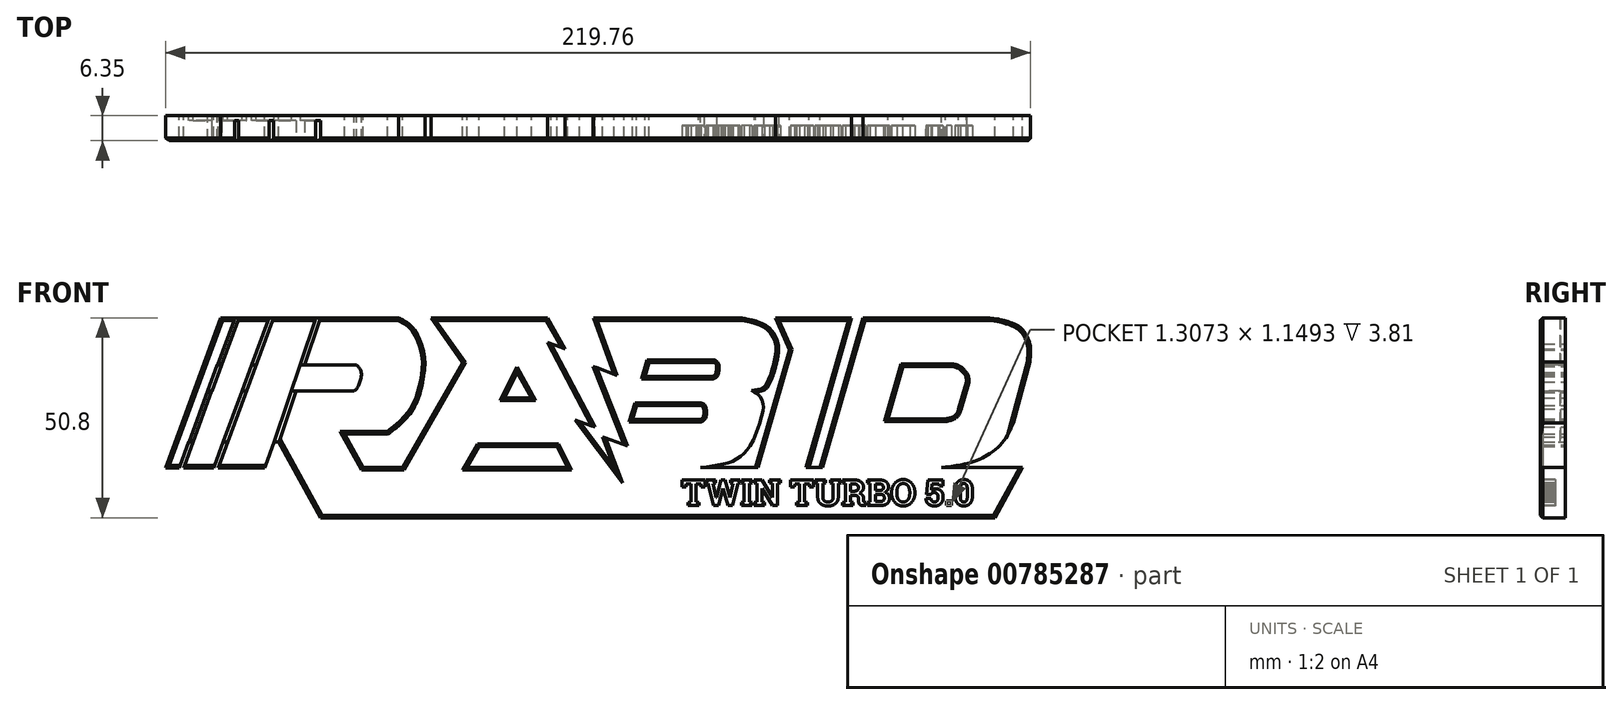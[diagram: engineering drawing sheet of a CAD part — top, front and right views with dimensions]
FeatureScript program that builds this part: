
annotation { "Feature Type Name" : "Feature", "Feature Type Description" : "" }
export const myFeature = defineFeature(function(context is Context, id is Id, definition is map)
    precondition{}
    {
        {
            var Q0;
            Q0=qCreatedBy(makeId("Front.planeOp"),FACE);
            var sketch = newSketch(context, id + "F0", { "sketchPlane" : qUnion([Q0])});
            skLineSegment(sketch, "E0", {"start": v(44.45, 18.23) * mm, "end": v(13.33, 18.23) * mm});
            skLineSegment(sketch, "E1", {"start": v(-163.82, -19.93) * mm, "end": v(-149.78, 18.23) * mm});
            skLineSegment(sketch, "E2", {"start": v(-138.67, -19.93) * mm, "end": v(-150.42, -19.93) * mm});
            skLineSegment(sketch, "E3", {"start": v(-146.28, 18.23) * mm, "end": v(-160.32, -19.93) * mm});
            skLineSegment(sketch, "E4", {"start": v(-159.23, -19.93) * mm, "end": v(-145.19, 18.23) * mm});
            skLineSegment(sketch, "E5", {"start": v(-137.53, 18.23) * mm, "end": v(-151.57, -19.93) * mm});
            skLineSegment(sketch, "E6", {"start": v(-150.42, -19.93) * mm, "end": v(-136.37, 18.23) * mm});
            skLineSegment(sketch, "E7", {"start": v(-124.63, 18.23) * mm, "end": v(-138.67, -19.93) * mm});
            skLineSegment(sketch, "E8", {"start": v(-127.97, 6.26) * mm, "end": v(-123.56, 18.23) * mm});
            skLineSegment(sketch, "E9", {"start": v(-127.97, 6.26) * mm, "end": v(-115.24, 6.26) * mm});
            skLineSegment(sketch, "E10", {"start": v(-115.92, -0.4) * mm, "end": v(-130.28, -0.4) * mm});
            skLineSegment(sketch, "E11", {"start": v(-130.28, -0.4) * mm, "end": v(-135.05, -13.36) * mm});
            skLineSegment(sketch, "E12", {"start": v(-135.05, -13.36) * mm, "end": v(-124.47, -32.57) * mm});
            skLineSegment(sketch, "E13", {"start": v(-124.47, -32.57) * mm, "end": v(-110.55, -32.57) * mm});
            skLineSegment(sketch, "E14", {"start": v(-110.55, -32.57) * mm, "end": v(-103.65, -19.74) * mm});
            skLineSegment(sketch, "E15", {"start": v(-103.65, -19.74) * mm, "end": v(-113.7, -19.74) * mm});
            skLineSegment(sketch, "E16", {"start": v(-113.7, -19.74) * mm, "end": v(-118.36, -11.28) * mm});
            skLineSegment(sketch, "E17", {"start": v(-118.36, -11.28) * mm, "end": v(-107.38, -11.28) * mm});
            skLineSegment(sketch, "E18", {"start": v(-103.65, -19.74) * mm, "end": v(-87.29, -19.74) * mm});
            skLineSegment(sketch, "E19", {"start": v(-96.42, 18.23) * mm, "end": v(-88.35, 6.81) * mm});
            skLineSegment(sketch, "E20", {"start": v(-88.35, 6.81) * mm, "end": v(-103.65, -19.74) * mm});
            skLineSegment(sketch, "E21", {"start": v(-87.29, -19.74) * mm, "end": v(-84.2, -14.4) * mm});
            skLineSegment(sketch, "E22", {"start": v(-84.2, -14.4) * mm, "end": v(-64.33, -14.4) * mm});
            skLineSegment(sketch, "E23", {"start": v(-64.33, -14.4) * mm, "end": v(-61.66, -19.74) * mm});
            skLineSegment(sketch, "E24", {"start": v(-66.84, 18.23) * mm, "end": v(-62.3, 10.3) * mm});
            skLineSegment(sketch, "E25", {"start": v(-62.3, 10.3) * mm, "end": v(-65.92, 11.65) * mm});
            skLineSegment(sketch, "E26", {"start": v(-65.92, 11.65) * mm, "end": v(-54.7, -9.5) * mm});
            skLineSegment(sketch, "E27", {"start": v(-54.7, -9.5) * mm, "end": v(-58.68, -8.06) * mm});
            skLineSegment(sketch, "E28", {"start": v(-58.68, -8.06) * mm, "end": v(-49.86, -19.74) * mm});
            skLineSegment(sketch, "E29", {"start": v(-70.89, -2.18) * mm, "end": v(-77.76, -2.18) * mm});
            skLineSegment(sketch, "E30", {"start": v(-77.76, -2.18) * mm, "end": v(-74.5, 4.32) * mm});
            skLineSegment(sketch, "E31", {"start": v(-74.5, 4.32) * mm, "end": v(-70.89, -2.18) * mm});
            skLineSegment(sketch, "E32", {"start": v(-55.14, 18.23) * mm, "end": v(-49.92, 3.87) * mm});
            skLineSegment(sketch, "E33", {"start": v(-49.92, 3.87) * mm, "end": v(-55.16, 5.86) * mm});
            skLineSegment(sketch, "E34", {"start": v(-55.16, 5.86) * mm, "end": v(-47.3, -14.02) * mm});
            skLineSegment(sketch, "E35", {"start": v(-47.3, -14.02) * mm, "end": v(-52.8, -12.04) * mm});
            skLineSegment(sketch, "E36", {"start": v(-52.8, -12.04) * mm, "end": v(-49.86, -19.74) * mm});
            skLineSegment(sketch, "E37", {"start": v(-40.97, 6.88) * mm, "end": v(-42, 3.36) * mm});
            skLineSegment(sketch, "E38", {"start": v(-45.2, -7.65) * mm, "end": v(-28.43, -7.65) * mm});
            skLineSegment(sketch, "E39", {"start": v(-44.14, -3.97) * mm, "end": v(-28.03, -3.97) * mm});
            skLineSegment(sketch, "E40", {"start": v(-40.97, 6.88) * mm, "end": v(-24.6, 6.88) * mm});
            skLineSegment(sketch, "E41", {"start": v(-42, 3.36) * mm, "end": v(-25, 3.36) * mm});
            skLineSegment(sketch, "E42", {"start": v(-8.93, 18.23) * mm, "end": v(-5.34, 10.12) * mm});
            skLineSegment(sketch, "E43", {"start": v(-5.34, 10.12) * mm, "end": v(-13.99, -19.74) * mm});
            skLineSegment(sketch, "E44", {"start": v(10.46, 18.23) * mm, "end": v(-0.4, -19.74) * mm});
            skLineSegment(sketch, "E45", {"start": v(13.33, 18.23) * mm, "end": v(2.47, -19.74) * mm});
            skLineSegment(sketch, "E46", {"start": v(35.81, 5.9) * mm, "end": v(23.48, 5.9) * mm});
            skLineSegment(sketch, "E47", {"start": v(23.48, 5.9) * mm, "end": v(19.66, -7.49) * mm});
            skLineSegment(sketch, "E48", {"start": v(19.66, -7.49) * mm, "end": v(34.3, -7.49) * mm});
            skLineSegment(sketch, "E49", {"start": v(39.6, 1.92) * mm, "end": v(37.65, -4.94) * mm});
            skFitSpline(sketch, "E50", {"points": [v(55.73, 7.05) * mm, v(55.73, 11.7) * mm, v(53.74, 15.4) * mm, v(50.9, 17) * mm, v(44.45, 18.23) * mm], "startDerivative": vector(2.3, 18.78) * mm, "endDerivative": vector(-24.45, 0) * mm});
            skLineSegment(sketch, "E51", {"start": v(55.73, 7.05) * mm, "end": v(51.56, -8.5) * mm});
            skFitSpline(sketch, "E52", {"points": [v(-14.17, -0.73) * mm, v(-12.02, -0.26) * mm, v(-10.54, 1.23) * mm, v(-8.14, 9.39) * mm, v(-8.72, 13.21) * mm, v(-10.35, 15.5) * mm, v(-13.7, 17.35) * mm, v(-18.93, 18.23) * mm], "startDerivative": vector(20.2, 3.41) * mm, "endDerivative": vector(-28.09, 0) * mm});
            skFitSpline(sketch, "E53", {"points": [v(-14.17, -0.73) * mm, v(-12.8, -1.84) * mm, v(-11.95, -3.81) * mm, v(-12.1, -5.72) * mm, v(-14.99, -13.75) * mm, v(-17.24, -16.5) * mm, v(-19.85, -18.27) * mm, v(-23.1, -19.11) * mm, v(-27.89, -19.74) * mm], "startDerivative": vector(16.43, -10.07) * mm, "endDerivative": vector(-33.98, 0) * mm});
            skFitSpline(sketch, "E54", {"points": [v(-24.6, 6.88) * mm, v(-24.2, 6.68) * mm, v(-23.87, 6.14) * mm, v(-24.05, 4.06) * mm, v(-24.29, 3.61) * mm, v(-25, 3.36) * mm], "startDerivative": vector(3.09, 0) * mm, "endDerivative": vector(-4.49, 0) * mm});
            skFitSpline(sketch, "E55", {"points": [v(-28.03, -3.97) * mm, v(-27.5, -4.2) * mm, v(-27.12, -4.85) * mm, v(-27.1, -6.65) * mm, v(-27.44, -7.25) * mm, v(-28.43, -7.65) * mm], "startDerivative": vector(3.73, 0) * mm, "endDerivative": vector(-8.7, -0.89) * mm});
            skFitSpline(sketch, "E56", {"points": [v(-104.57, 18.23) * mm, v(-101.7, 16.39) * mm, v(-99.55, 13.37) * mm, v(-98.04, 8.28) * mm, v(-98.33, 2.83) * mm, v(-99.98, -3.05) * mm, v(-103.2, -7.86) * mm, v(-107.38, -11.28) * mm], "startDerivative": vector(25.95, -13.02) * mm, "endDerivative": vector(-29.28, -21.25) * mm});
            skFitSpline(sketch, "E57", {"points": [v(35.81, 5.9) * mm, v(37.17, 5.6) * mm, v(38.23, 4.97) * mm, v(39.07, 4.03) * mm, v(39.6, 1.92) * mm], "startDerivative": vector(5.58, 0) * mm, "endDerivative": vector(-1.33, -10.82) * mm});
            skFitSpline(sketch, "E58", {"points": [v(34.3, -7.49) * mm, v(35.48, -7.2) * mm, v(36.57, -6.77) * mm, v(37.26, -5.96) * mm, v(37.65, -4.94) * mm], "startDerivative": vector(4.57, 1.01) * mm, "endDerivative": vector(1.33, 4.26) * mm});
            skLineSegment(sketch, "E59.trimOffspring", {"start": v(-146.28, 18.23) * mm, "end": v(-149.78, 18.23) * mm});
            skLineSegment(sketch, "E60.trimOffspring", {"start": v(-137.53, 18.23) * mm, "end": v(-145.19, 18.23) * mm});
            skLineSegment(sketch, "E61.trimOffspring", {"start": v(-124.63, 18.23) * mm, "end": v(-136.37, 18.23) * mm});
            skLineSegment(sketch, "E62.trimOffspring", {"start": v(-104.57, 18.23) * mm, "end": v(-123.56, 18.23) * mm});
            skLineSegment(sketch, "E63.trimOffspring", {"start": v(-151.57, -19.93) * mm, "end": v(-159.23, -19.93) * mm});
            skLineSegment(sketch, "E64.trimOffspring", {"start": v(-160.32, -19.93) * mm, "end": v(-163.82, -19.93) * mm});
            skLineSegment(sketch, "E65.trimOffspring", {"start": v(-61.66, -19.74) * mm, "end": v(-49.86, -19.74) * mm});
            skLineSegment(sketch, "E66.trimOffspring", {"start": v(-49.86, -19.74) * mm, "end": v(-27.89, -19.74) * mm});
            skLineSegment(sketch, "E67.trimOffspring", {"start": v(-66.84, 18.23) * mm, "end": v(-96.42, 18.23) * mm});
            skLineSegment(sketch, "E68.trimOffspring", {"start": v(-44.14, -3.97) * mm, "end": v(-45.2, -7.65) * mm});
            skLineSegment(sketch, "E69.trimOffspring", {"start": v(-18.93, 18.23) * mm, "end": v(-55.14, 18.23) * mm});
            skLineSegment(sketch, "E70.trimOffspring", {"start": v(-13.99, -19.74) * mm, "end": v(-0.4, -19.74) * mm});
            skLineSegment(sketch, "E71.trimOffspring", {"start": v(2.47, -19.74) * mm, "end": v(33.3, -19.74) * mm});
            skLineSegment(sketch, "E72.trimOffspring", {"start": v(10.46, 18.23) * mm, "end": v(-8.93, 18.23) * mm});
            skFitSpline(sketch, "E73", {"points": [v(51.56, -8.5) * mm, v(50.36, -11.15) * mm, v(48.41, -13.9) * mm, v(45.57, -16.27) * mm, v(42.49, -17.92) * mm, v(38.84, -18.97) * mm, v(33.3, -19.74) * mm], "startDerivative": vector(-7.47, -18.05) * mm, "endDerivative": vector(-28.9, 0) * mm});
            skFitSpline(sketch, "E74", {"points": [v(-115.24, 6.26) * mm, v(-114.2, 4.72) * mm, v(-114.26, 2.54) * mm, v(-115.24, 0.25) * mm, v(-115.92, -0.4) * mm], "startDerivative": vector(5.02, -5.67) * mm, "endDerivative": vector(-3.78, -2.78) * mm});
            skLineSegment(sketch, "E75", {"start": v(-87.29, -19.74) * mm, "end": v(-61.66, -19.74) * mm});
            skLineSegment(sketch, "E76", {"start": v(-27.89, -19.74) * mm, "end": v(-13.99, -19.74) * mm});
            skLineSegment(sketch, "E77", {"start": v(-0.4, -19.74) * mm, "end": v(2.47, -19.74) * mm});
            skLineSegment(sketch, "E78", {"start": v(27.98, -32.57) * mm, "end": v(-110.55, -32.57) * mm});
            skLineSegment(sketch, "E79", {"start": v(27.98, -32.57) * mm, "end": v(46.92, -32.57) * mm});
            skLineSegment(sketch, "E80", {"start": v(46.92, -32.57) * mm, "end": v(53.92, -19.74) * mm});
            skLineSegment(sketch, "E81", {"start": v(33.3, -19.74) * mm, "end": v(53.92, -19.74) * mm});
            skLineSegment(sketch, "E82", {"start": v(-123.56, 18.23) * mm, "end": v(-124.63, 18.23) * mm});
            skLineSegment(sketch, "E83", {"start": v(-136.37, 18.23) * mm, "end": v(-137.53, 18.23) * mm});
            skLineSegment(sketch, "E84", {"start": v(-127.97, 6.26) * mm, "end": v(-129.04, 6.26) * mm});
            skLineSegment(sketch, "E85", {"start": v(-130.28, -0.4) * mm, "end": v(-131.49, -0.4) * mm});
            skLineSegment(sketch, "E86", {"start": v(-145.19, 18.23) * mm, "end": v(-146.28, 18.23) * mm});
            skLineSegment(sketch, "E87", {"start": v(-140.78, 6.26) * mm, "end": v(-141.94, 6.26) * mm});
            skLineSegment(sketch, "E88", {"start": v(-149.6, 6.26) * mm, "end": v(-150.69, 6.26) * mm});
            skLineSegment(sketch, "E89", {"start": v(-143.23, -0.4) * mm, "end": v(-144.39, -0.4) * mm});
            skLineSegment(sketch, "E90", {"start": v(-152.05, -0.4) * mm, "end": v(-153.14, -0.4) * mm});
            skLineSegment(sketch, "E91", {"start": v(-130.28, -0.4) * mm, "end": v(-127.97, 6.26) * mm});
            skLineSegment(sketch, "E92", {"start": v(-135.05, -13.36) * mm, "end": v(-136.25, -13.36) * mm});
            skLineSegment(sketch, "E93", {"start": v(-148, -13.36) * mm, "end": v(-149.15, -13.36) * mm});
            skLineSegment(sketch, "E94", {"start": v(-156.81, -13.36) * mm, "end": v(-157.9, -13.36) * mm});
            skSolve(sketch);
        }
        {
            var Q0;
            Q0=qSketchRegion(id+"F0",true);
            extrude(context, id + "F1", {"entities" : qUnion([Q0]), "depth" : 6.35 * mm, "offsetDistance" : 25.4 * mm});
        }
        {
            var Q0;
            {var subQ0=sQuery(id+"F0.wireOp",EDGE,"E30");var subQ1=sQuery(id+"F0.wireOp",EDGE,"E29");var subQ2=sQuery(id+"F0.wireOp",EDGE,"E27");var subQ3=sQuery(id+"F0.wireOp",EDGE,"E24");var subQ4=sQuery(id+"F0.wireOp",EDGE,"E23");var subQ5=sQuery(id+"F0.wireOp",EDGE,"E22");var subQ6=sQuery(id+"F0.wireOp",EDGE,"E21");var subQ7=sQuery(id+"F0.wireOp",EDGE,"E20");var subQ8=sQuery(id+"F0.wireOp",EDGE,"E19");var subQ9=sQuery(id+"F0.wireOp",EDGE,"E17");var subQ10=sQuery(id+"F0.wireOp",EDGE,"E16");var subQ11=sQuery(id+"F0.wireOp",EDGE,"E15");var subQ12=sQuery(id+"F0.wireOp",EDGE,"E79");var subQ13=sQuery(id+"F0.wireOp",EDGE,"E78");var subQ14=sQuery(id+"F0.wireOp",EDGE,"E13");var subQ15=sQuery(id+"F0.wireOp",EDGE,"E12");var subQ16=sQuery(id+"F0.wireOp",EDGE,"E85");var subQ17=sQuery(id+"F0.wireOp",EDGE,"E10");var subQ18=sQuery(id+"F0.wireOp",EDGE,"E84");var subQ19=sQuery(id+"F0.wireOp",EDGE,"E9");var subQ20=sQuery(id+"F0.wireOp",EDGE,"E7");var subQ21=sQuery(id+"F0.wireOp",EDGE,"E2");var subQ22=sQuery(id+"F0.wireOp",EDGE,"E92");var subQ23=sQuery(id+"F0.wireOp",EDGE,"E87");var subQ24=sQuery(id+"F0.wireOp",EDGE,"E6");var subQ25=sQuery(id+"F0.wireOp",EDGE,"E89");var subQ26=sQuery(id+"F0.wireOp",EDGE,"E93");var subQ27=sQuery(id+"F0.wireOp",EDGE,"E63.trimOffspring");var subQ28=sQuery(id+"F0.wireOp",EDGE,"E5");var subQ29=sQuery(id+"F0.wireOp",EDGE,"E88");var subQ30=sQuery(id+"F0.wireOp",EDGE,"E4");var subQ31=sQuery(id+"F0.wireOp",EDGE,"E90");var subQ32=sQuery(id+"F0.wireOp",EDGE,"E94");var subQ33=sQuery(id+"F0.wireOp",EDGE,"E64.trimOffspring");var subQ34=sQuery(id+"F0.wireOp",EDGE,"E3");var subQ35=sQuery(id+"F0.wireOp",EDGE,"E1");var subQ36=sQuery(id+"F0.wireOp",EDGE,"E0");var subQ37=sQuery(id+"F0.wireOp",EDGE,"E81");var subQ38=sQuery(id+"F0.wireOp",EDGE,"E80");var subQ39=sQuery(id+"F0.wireOp",EDGE,"E76");var subQ40=sQuery(id+"F0.wireOp",EDGE,"E75");var subQ41=sQuery(id+"F0.wireOp",EDGE,"E74");var subQ42=sQuery(id+"F0.wireOp",EDGE,"E73");var subQ43=sQuery(id+"F0.wireOp",EDGE,"E72.trimOffspring");var subQ44=sQuery(id+"F0.wireOp",EDGE,"E69.trimOffspring");var subQ45=sQuery(id+"F0.wireOp",EDGE,"E68.trimOffspring");var subQ46=sQuery(id+"F0.wireOp",EDGE,"E48");var subQ47=sQuery(id+"F0.wireOp",EDGE,"E77");var subQ48=sQuery(id+"F0.wireOp",EDGE,"E47");var subQ49=sQuery(id+"F0.wireOp",EDGE,"E45");var subQ50=sQuery(id+"F0.wireOp",EDGE,"E50");var subQ51=sQuery(id+"F0.wireOp",EDGE,"E28");var subQ52=sQuery(id+"F0.wireOp",EDGE,"E49");var subQ53=sQuery(id+"F0.wireOp",EDGE,"E46");var subQ54=sQuery(id+"F0.wireOp",EDGE,"E55");var subQ55=sQuery(id+"F0.wireOp",EDGE,"E41");var subQ56=sQuery(id+"F0.wireOp",EDGE,"E40");var subQ57=sQuery(id+"F0.wireOp",EDGE,"E32");var subQ58=sQuery(id+"F0.wireOp",EDGE,"E31");var subQ59=sQuery(id+"F0.wireOp",EDGE,"E33");var subQ60=sQuery(id+"F0.wireOp",EDGE,"E51");var subQ61=sQuery(id+"F0.wireOp",EDGE,"E44");var subQ62=sQuery(id+"F0.wireOp",EDGE,"E39");var subQ63=sQuery(id+"F0.wireOp",EDGE,"E34");var subQ64=sQuery(id+"F0.wireOp",EDGE,"E35");var subQ65=sQuery(id+"F0.wireOp",EDGE,"E36");var subQ66=sQuery(id+"F0.wireOp",EDGE,"E37");var subQ67=sQuery(id+"F0.wireOp",EDGE,"E38");var subQ68=sQuery(id+"F0.wireOp",EDGE,"E52");var subQ69=sQuery(id+"F0.wireOp",EDGE,"E53");var subQ70=sQuery(id+"F0.wireOp",EDGE,"E54");var subQ71=sQuery(id+"F0.wireOp",EDGE,"E56");var subQ72=sQuery(id+"F0.wireOp",EDGE,"E25");var subQ73=sQuery(id+"F0.wireOp",EDGE,"E57");var subQ74=sQuery(id+"F0.wireOp",EDGE,"E26");var subQ75=sQuery(id+"F0.wireOp",EDGE,"E58");var subQ76=sQuery(id+"F0.wireOp",EDGE,"E86");var subQ77=sQuery(id+"F0.wireOp",EDGE,"E83");var subQ78=sQuery(id+"F0.wireOp",EDGE,"E82");var subQ79=sQuery(id+"F0.wireOp",EDGE,"E62.trimOffspring");var subQ80=sQuery(id+"F0.wireOp",EDGE,"E61.trimOffspring");var subQ81=sQuery(id+"F0.wireOp",EDGE,"E60.trimOffspring");var subQ82=sQuery(id+"F0.wireOp",EDGE,"E59.trimOffspring");var subQ83=sQuery(id+"F0.wireOp",EDGE,"E67.trimOffspring");var subQ84=sQuery(id+"F0.wireOp",EDGE,"E42");var subQ85=sQuery(id+"F0.wireOp",EDGE,"E43");Q0=makeQuery(id+"F5.boolean.opBoolean","SPLIT",FACE,{"disambiguationData":[TD([makeQuery(id+"F1.opExtrude","SWEPT_FACE",FACE,{"disambiguationData":[OSD([subQ36])]})])],"derivedFrom":makeQuery(id+"F1.opExtrude","CAP_FACE",FACE,{"disambiguationData":[OSD([subQ36,subQ35,subQ21,subQ34,subQ30,subQ28,subQ24,subQ20,subQ19,subQ17,subQ15,subQ14,subQ11,subQ10,subQ9,subQ8,subQ7,subQ6,subQ5,subQ4,subQ3,subQ72,subQ74,subQ2,subQ51,subQ1,subQ0,subQ58,subQ57,subQ59,subQ63,subQ64,subQ65,subQ66,subQ67,subQ62,subQ56,subQ55,subQ84,subQ85,subQ61,subQ49,subQ53,subQ48,subQ46,subQ52,subQ50,subQ60,subQ68,subQ69,subQ70,subQ54,subQ71,subQ73,subQ75,subQ82,subQ81,subQ80,subQ79,subQ27,subQ33,subQ83,subQ45,subQ44,subQ43,subQ42,subQ41,subQ40,subQ39,subQ47,subQ13,subQ12,subQ38,subQ37,subQ78,subQ77,subQ18,subQ16,subQ76,subQ23,subQ29,subQ25,subQ31,subQ22,subQ26,subQ32])],"isStart":false})});}
            var sketch = newSketch(context, id + "F2", { "sketchPlane" : qUnion([Q0])});
            skLineSegment(sketch, "E95", {"start": v(-160.32, -19.93) * mm, "end": v(-159.23, -19.93) * mm});
            skLineSegment(sketch, "E96", {"start": v(-159.23, -19.93) * mm, "end": v(-145.22, 18.23) * mm});
            skLineSegment(sketch, "E97", {"start": v(-145.22, 18.23) * mm, "end": v(-146.23, 18.23) * mm});
            skLineSegment(sketch, "E98", {"start": v(-146.23, 18.23) * mm, "end": v(-160.32, -19.93) * mm});
            skLineSegment(sketch, "E99", {"start": v(-151.57, -19.93) * mm, "end": v(-150.42, -19.93) * mm});
            skLineSegment(sketch, "E100", {"start": v(-150.42, -19.93) * mm, "end": v(-136.37, 18.23) * mm});
            skLineSegment(sketch, "E101", {"start": v(-136.37, 18.23) * mm, "end": v(-137.53, 18.23) * mm});
            skLineSegment(sketch, "E102", {"start": v(-137.53, 18.23) * mm, "end": v(-151.57, -19.93) * mm});
            skPoint(sketch, "E103.endSnap0", {"position": v(-129.76, -22.96) * mm});
            skLineSegment(sketch, "E104", {"start": v(-136.25, -13.36) * mm, "end": v(-135.05, -13.36) * mm});
            skLineSegment(sketch, "E105", {"start": v(-135.05, -13.36) * mm, "end": v(-124.47, 18.23) * mm});
            skLineSegment(sketch, "E106", {"start": v(-124.47, 18.23) * mm, "end": v(-125.67, 18.23) * mm});
            skLineSegment(sketch, "E107", {"start": v(-125.67, 18.23) * mm, "end": v(-136.25, -13.36) * mm});
            skSolve(sketch);
        }
        {
            var Q0;
            Q0=qSketchRegion(id+"F2",true);
            extrude(context, id + "F3", {"entities" : qUnion([Q0]), "operationType" : NewBodyOperationType.REMOVE, "oppositeDirection" : true, "depth" : 5.08 * mm, "offsetDistance" : 25.4 * mm});
        }
        {
            var Q0;
            Q0=makeQuery(id+"F1.opExtrude","CAP_FACE",FACE,{"disambiguationData":[OSD([sQuery(id+"F0.wireOp",EDGE,"E0"),sQuery(id+"F0.wireOp",EDGE,"E8"),sQuery(id+"F0.wireOp",EDGE,"E9"),sQuery(id+"F0.wireOp",EDGE,"E10"),sQuery(id+"F0.wireOp",EDGE,"E11"),sQuery(id+"F0.wireOp",EDGE,"E12"),sQuery(id+"F0.wireOp",EDGE,"E13"),sQuery(id+"F0.wireOp",EDGE,"E15"),sQuery(id+"F0.wireOp",EDGE,"E16"),sQuery(id+"F0.wireOp",EDGE,"E17"),sQuery(id+"F0.wireOp",EDGE,"E19"),sQuery(id+"F0.wireOp",EDGE,"E20"),sQuery(id+"F0.wireOp",EDGE,"E21"),sQuery(id+"F0.wireOp",EDGE,"E22"),sQuery(id+"F0.wireOp",EDGE,"E23"),sQuery(id+"F0.wireOp",EDGE,"E24"),sQuery(id+"F0.wireOp",EDGE,"E25"),sQuery(id+"F0.wireOp",EDGE,"E26"),sQuery(id+"F0.wireOp",EDGE,"E27"),sQuery(id+"F0.wireOp",EDGE,"E28"),sQuery(id+"F0.wireOp",EDGE,"E29"),sQuery(id+"F0.wireOp",EDGE,"E30"),sQuery(id+"F0.wireOp",EDGE,"E31"),sQuery(id+"F0.wireOp",EDGE,"E32"),sQuery(id+"F0.wireOp",EDGE,"E33"),sQuery(id+"F0.wireOp",EDGE,"E34"),sQuery(id+"F0.wireOp",EDGE,"E35"),sQuery(id+"F0.wireOp",EDGE,"E36"),sQuery(id+"F0.wireOp",EDGE,"E37"),sQuery(id+"F0.wireOp",EDGE,"E38"),sQuery(id+"F0.wireOp",EDGE,"E39"),sQuery(id+"F0.wireOp",EDGE,"E40"),sQuery(id+"F0.wireOp",EDGE,"E41"),sQuery(id+"F0.wireOp",EDGE,"E42"),sQuery(id+"F0.wireOp",EDGE,"E43"),sQuery(id+"F0.wireOp",EDGE,"E44"),sQuery(id+"F0.wireOp",EDGE,"E45"),sQuery(id+"F0.wireOp",EDGE,"E46"),sQuery(id+"F0.wireOp",EDGE,"E47"),sQuery(id+"F0.wireOp",EDGE,"E48"),sQuery(id+"F0.wireOp",EDGE,"E49"),sQuery(id+"F0.wireOp",EDGE,"E50"),sQuery(id+"F0.wireOp",EDGE,"E51"),sQuery(id+"F0.wireOp",EDGE,"E52"),sQuery(id+"F0.wireOp",EDGE,"E53"),sQuery(id+"F0.wireOp",EDGE,"E54"),sQuery(id+"F0.wireOp",EDGE,"E55"),sQuery(id+"F0.wireOp",EDGE,"E56"),sQuery(id+"F0.wireOp",EDGE,"E57"),sQuery(id+"F0.wireOp",EDGE,"E58"),sQuery(id+"F0.wireOp",EDGE,"E62.trimOffspring"),sQuery(id+"F0.wireOp",EDGE,"E67.trimOffspring"),sQuery(id+"F0.wireOp",EDGE,"E68.trimOffspring"),sQuery(id+"F0.wireOp",EDGE,"E69.trimOffspring"),sQuery(id+"F0.wireOp",EDGE,"E72.trimOffspring"),sQuery(id+"F0.wireOp",EDGE,"E73"),sQuery(id+"F0.wireOp",EDGE,"E74"),sQuery(id+"F0.wireOp",EDGE,"E75"),sQuery(id+"F0.wireOp",EDGE,"E76"),sQuery(id+"F0.wireOp",EDGE,"E77"),sQuery(id+"F0.wireOp",EDGE,"ISSC0bJT-fq30-P4vY-vGbu-V4KtggNEUtfu"),sQuery(id+"F0.wireOp",EDGE,"E78")])],"isStart":false});
            var sketch = newSketch(context, id + "F4", { "sketchPlane" : qUnion([Q0])});
            skText(sketch, "E108", { "text": "TWIN TURBO 5.0", "fontName": "RobotoSlab-Bold.ttf"});
            const initialGuessF4  = {"E108": [-0.0328, -0.02948, 1, 0, 0.00662]};
            skSetInitialGuess(sketch, initialGuessF4);
            skSolve(sketch);
        }
        {
            var Q0;
            Q0=qSketchRegion(id+"F4",true);
            extrude(context, id + "F5", {"entities" : qUnion([Q0]), "operationType" : NewBodyOperationType.REMOVE, "oppositeDirection" : true, "depth" : 3.8 * mm, "offsetDistance" : 25.4 * mm});
        }
        {
            var Q0;
            {var subQ0=sQuery(id+"F0.wireOp",EDGE,"E86");var subQ1=sQuery(id+"F0.wireOp",EDGE,"E83");var subQ2=sQuery(id+"F0.wireOp",EDGE,"E82");var subQ3=sQuery(id+"F0.wireOp",EDGE,"E62.trimOffspring");var subQ4=sQuery(id+"F0.wireOp",EDGE,"E61.trimOffspring");var subQ5=sQuery(id+"F0.wireOp",EDGE,"E60.trimOffspring");var subQ6=sQuery(id+"F0.wireOp",EDGE,"E59.trimOffspring");var subQ7=sQuery(id+"F0.wireOp",EDGE,"E1");Q0=makeQuery(id+"F3.boolean.opBoolean","SPLIT",EDGE,{"disambiguationData":[TD([makeQuery(id+"F1.opExtrude","SWEPT_FACE",FACE,{"disambiguationData":[OSD([subQ7])]})])],"derivedFrom":makeQuery(id+"F1.opExtrude","CAP_EDGE",EDGE,{"disambiguationData":[OSD([subQ6,subQ5,subQ4,subQ3,subQ2,subQ1,subQ0])],"isStart":false})});}
            var Q1;
            {var subQ0=sQuery(id+"F0.wireOp",EDGE,"E86");var subQ1=sQuery(id+"F0.wireOp",EDGE,"E83");var subQ2=sQuery(id+"F0.wireOp",EDGE,"E82");var subQ3=sQuery(id+"F0.wireOp",EDGE,"E62.trimOffspring");var subQ4=sQuery(id+"F0.wireOp",EDGE,"E61.trimOffspring");var subQ5=sQuery(id+"F0.wireOp",EDGE,"E60.trimOffspring");var subQ6=sQuery(id+"F0.wireOp",EDGE,"E59.trimOffspring");Q1=makeQuery(id+"F3.boolean.opBoolean","SPLIT",EDGE,{"disambiguationData":[TD([makeQuery(id+"F3.opExtrude","SWEPT_FACE",FACE,{"disambiguationData":[OSD([sQuery(id+"F2.wireOp",EDGE,"E96")])]})])],"derivedFrom":makeQuery(id+"F1.opExtrude","CAP_EDGE",EDGE,{"disambiguationData":[OSD([subQ6,subQ5,subQ4,subQ3,subQ2,subQ1,subQ0])],"isStart":false})});}
            var Q2;
            Q2=makeQuery(id+"F1.opExtrude","CAP_EDGE",EDGE,{"disambiguationData":[OSD([sQuery(id+"F0.wireOp",EDGE,"E2")])],"isStart":false});
            var Q3;
            Q3=makeQuery(id+"F1.opExtrude","CAP_EDGE",EDGE,{"disambiguationData":[OSD([sQuery(id+"F0.wireOp",EDGE,"E63.trimOffspring")])],"isStart":false});
            var Q4;
            Q4=makeQuery(id+"F1.opExtrude","CAP_EDGE",EDGE,{"disambiguationData":[OSD([sQuery(id+"F0.wireOp",EDGE,"E64.trimOffspring")])],"isStart":false});
            var Q5;
            Q5=makeQuery(id+"F1.opExtrude","CAP_EDGE",EDGE,{"disambiguationData":[OSD([sQuery(id+"F0.wireOp",EDGE,"E1")])],"isStart":false});
            var Q6;
            {var subQ0=sQuery(id+"F0.wireOp",EDGE,"E86");var subQ1=sQuery(id+"F0.wireOp",EDGE,"E83");var subQ2=sQuery(id+"F0.wireOp",EDGE,"E82");var subQ3=sQuery(id+"F0.wireOp",EDGE,"E62.trimOffspring");var subQ4=sQuery(id+"F0.wireOp",EDGE,"E61.trimOffspring");var subQ5=sQuery(id+"F0.wireOp",EDGE,"E60.trimOffspring");var subQ6=sQuery(id+"F0.wireOp",EDGE,"E59.trimOffspring");var subQ7=sQuery(id+"F0.wireOp",EDGE,"E56");Q6=makeQuery(id+"F3.boolean.opBoolean","SPLIT",EDGE,{"disambiguationData":[TD([makeQuery(id+"F1.opExtrude","SWEPT_FACE",FACE,{"disambiguationData":[OSD([subQ7])]})])],"derivedFrom":makeQuery(id+"F1.opExtrude","CAP_EDGE",EDGE,{"disambiguationData":[OSD([subQ6,subQ5,subQ4,subQ3,subQ2,subQ1,subQ0])],"isStart":false})});}
            var Q7;
            Q7=makeQuery(id+"F1.opExtrude","CAP_EDGE",EDGE,{"disambiguationData":[OSD([sQuery(id+"F0.wireOp",EDGE,"E56")])],"isStart":false});
            var Q8;
            Q8=makeQuery(id+"F1.opExtrude","CAP_EDGE",EDGE,{"disambiguationData":[OSD([sQuery(id+"F0.wireOp",EDGE,"E17")])],"isStart":false});
            var Q9;
            Q9=makeQuery(id+"F1.opExtrude","CAP_EDGE",EDGE,{"disambiguationData":[OSD([sQuery(id+"F0.wireOp",EDGE,"E16")])],"isStart":false});
            var Q10;
            Q10=makeQuery(id+"F1.opExtrude","CAP_EDGE",EDGE,{"disambiguationData":[OSD([sQuery(id+"F0.wireOp",EDGE,"E15")])],"isStart":false});
            var Q11;
            Q11=makeQuery(id+"F1.opExtrude","CAP_EDGE",EDGE,{"disambiguationData":[OSD([sQuery(id+"F0.wireOp",EDGE,"E20")])],"isStart":false});
            var Q12;
            Q12=makeQuery(id+"F1.opExtrude","CAP_EDGE",EDGE,{"disambiguationData":[OSD([sQuery(id+"F0.wireOp",EDGE,"E19")])],"isStart":false});
            var Q13;
            Q13=makeQuery(id+"F1.opExtrude","CAP_EDGE",EDGE,{"disambiguationData":[OSD([sQuery(id+"F0.wireOp",EDGE,"E67.trimOffspring")])],"isStart":false});
            var Q14;
            Q14=makeQuery(id+"F1.opExtrude","CAP_EDGE",EDGE,{"disambiguationData":[OSD([sQuery(id+"F0.wireOp",EDGE,"E24")])],"isStart":false});
            var Q15;
            Q15=makeQuery(id+"F1.opExtrude","CAP_EDGE",EDGE,{"disambiguationData":[OSD([sQuery(id+"F0.wireOp",EDGE,"E28")])],"isStart":false});
            var Q16;
            Q16=makeQuery(id+"F1.opExtrude","CAP_EDGE",EDGE,{"disambiguationData":[OSD([sQuery(id+"F0.wireOp",EDGE,"E36")])],"isStart":false});
            var Q17;
            Q17=makeQuery(id+"F1.opExtrude","CAP_EDGE",EDGE,{"disambiguationData":[OSD([sQuery(id+"F0.wireOp",EDGE,"E34")])],"isStart":false});
            var Q18;
            Q18=makeQuery(id+"F1.opExtrude","CAP_EDGE",EDGE,{"disambiguationData":[OSD([sQuery(id+"F0.wireOp",EDGE,"E32")])],"isStart":false});
            var Q19;
            Q19=makeQuery(id+"F1.opExtrude","CAP_EDGE",EDGE,{"disambiguationData":[OSD([sQuery(id+"F0.wireOp",EDGE,"E69.trimOffspring")])],"isStart":false});
            var Q20;
            Q20=makeQuery(id+"F1.opExtrude","CAP_EDGE",EDGE,{"disambiguationData":[OSD([sQuery(id+"F0.wireOp",EDGE,"E52")])],"isStart":false});
            var Q21;
            Q21=makeQuery(id+"F1.opExtrude","CAP_EDGE",EDGE,{"disambiguationData":[OSD([sQuery(id+"F0.wireOp",EDGE,"E43")])],"isStart":false});
            var Q22;
            Q22=makeQuery(id+"F1.opExtrude","CAP_EDGE",EDGE,{"disambiguationData":[OSD([sQuery(id+"F0.wireOp",EDGE,"E42")])],"isStart":false});
            var Q23;
            Q23=makeQuery(id+"F1.opExtrude","CAP_EDGE",EDGE,{"disambiguationData":[OSD([sQuery(id+"F0.wireOp",EDGE,"E72.trimOffspring")])],"isStart":false});
            var Q24;
            Q24=makeQuery(id+"F1.opExtrude","CAP_EDGE",EDGE,{"disambiguationData":[OSD([sQuery(id+"F0.wireOp",EDGE,"E44")])],"isStart":false});
            var Q25;
            Q25=makeQuery(id+"F1.opExtrude","CAP_EDGE",EDGE,{"disambiguationData":[OSD([sQuery(id+"F0.wireOp",EDGE,"E45")])],"isStart":false});
            var Q26;
            Q26=makeQuery(id+"F1.opExtrude","CAP_EDGE",EDGE,{"disambiguationData":[OSD([sQuery(id+"F0.wireOp",EDGE,"E0")])],"isStart":false});
            var Q27;
            Q27=makeQuery(id+"F1.opExtrude","CAP_EDGE",EDGE,{"disambiguationData":[OSD([sQuery(id+"F0.wireOp",EDGE,"E50")])],"isStart":false});
            var Q28;
            Q28=makeQuery(id+"F1.opExtrude","CAP_EDGE",EDGE,{"disambiguationData":[OSD([sQuery(id+"F0.wireOp",EDGE,"E51")])],"isStart":false});
            var Q29;
            Q29=makeQuery(id+"F1.opExtrude","CAP_EDGE",EDGE,{"disambiguationData":[OSD([sQuery(id+"F0.wireOp",EDGE,"E80")])],"isStart":false});
            var Q30;
            Q30=makeQuery(id+"F1.opExtrude","CAP_EDGE",EDGE,{"disambiguationData":[OSD([sQuery(id+"F0.wireOp",EDGE,"E13"),sQuery(id+"F0.wireOp",EDGE,"E78"),sQuery(id+"F0.wireOp",EDGE,"E79")])],"isStart":false});
            var Q31;
            Q31=makeQuery(id+"F1.opExtrude","CAP_EDGE",EDGE,{"disambiguationData":[OSD([sQuery(id+"F0.wireOp",EDGE,"E75")])],"isStart":false});
            var Q32;
            Q32=makeQuery(id+"F1.opExtrude","CAP_EDGE",EDGE,{"disambiguationData":[OSD([sQuery(id+"F0.wireOp",EDGE,"E23")])],"isStart":false});
            var Q33;
            Q33=makeQuery(id+"F1.opExtrude","CAP_EDGE",EDGE,{"disambiguationData":[OSD([sQuery(id+"F0.wireOp",EDGE,"E22")])],"isStart":false});
            var Q34;
            Q34=makeQuery(id+"F1.opExtrude","CAP_EDGE",EDGE,{"disambiguationData":[OSD([sQuery(id+"F0.wireOp",EDGE,"E21")])],"isStart":false});
            var Q35;
            Q35=makeQuery(id+"F1.opExtrude","CAP_EDGE",EDGE,{"disambiguationData":[OSD([sQuery(id+"F0.wireOp",EDGE,"E29")])],"isStart":false});
            var Q36;
            Q36=makeQuery(id+"F1.opExtrude","CAP_EDGE",EDGE,{"disambiguationData":[OSD([sQuery(id+"F0.wireOp",EDGE,"E31")])],"isStart":false});
            var Q37;
            Q37=makeQuery(id+"F1.opExtrude","CAP_EDGE",EDGE,{"disambiguationData":[OSD([sQuery(id+"F0.wireOp",EDGE,"E30")])],"isStart":false});
            var Q38;
            Q38=makeQuery(id+"F1.opExtrude","CAP_EDGE",EDGE,{"disambiguationData":[OSD([sQuery(id+"F0.wireOp",EDGE,"E38")])],"isStart":false});
            var Q39;
            Q39=makeQuery(id+"F1.opExtrude","CAP_EDGE",EDGE,{"disambiguationData":[OSD([sQuery(id+"F0.wireOp",EDGE,"E55")])],"isStart":false});
            var Q40;
            Q40=makeQuery(id+"F1.opExtrude","CAP_EDGE",EDGE,{"disambiguationData":[OSD([sQuery(id+"F0.wireOp",EDGE,"E68.trimOffspring")])],"isStart":false});
            var Q41;
            Q41=makeQuery(id+"F1.opExtrude","CAP_EDGE",EDGE,{"disambiguationData":[OSD([sQuery(id+"F0.wireOp",EDGE,"E41")])],"isStart":false});
            var Q42;
            Q42=makeQuery(id+"F1.opExtrude","CAP_EDGE",EDGE,{"disambiguationData":[OSD([sQuery(id+"F0.wireOp",EDGE,"E37")])],"isStart":false});
            var Q43;
            Q43=makeQuery(id+"F1.opExtrude","CAP_EDGE",EDGE,{"disambiguationData":[OSD([sQuery(id+"F0.wireOp",EDGE,"E26")])],"isStart":false});
            var Q44;
            Q44=makeQuery(id+"F1.opExtrude","CAP_EDGE",EDGE,{"disambiguationData":[OSD([sQuery(id+"F0.wireOp",EDGE,"E46")])],"isStart":false});
            var Q45;
            Q45=makeQuery(id+"F1.opExtrude","CAP_EDGE",EDGE,{"disambiguationData":[OSD([sQuery(id+"F0.wireOp",EDGE,"E57")])],"isStart":false});
            var Q46;
            Q46=makeQuery(id+"F1.opExtrude","CAP_EDGE",EDGE,{"disambiguationData":[OSD([sQuery(id+"F0.wireOp",EDGE,"E49")])],"isStart":false});
            var Q47;
            Q47=makeQuery(id+"F1.opExtrude","CAP_EDGE",EDGE,{"disambiguationData":[OSD([sQuery(id+"F0.wireOp",EDGE,"E58")])],"isStart":false});
            var Q48;
            Q48=makeQuery(id+"F1.opExtrude","CAP_EDGE",EDGE,{"disambiguationData":[OSD([sQuery(id+"F0.wireOp",EDGE,"E48")])],"isStart":false});
            var Q49;
            Q49=makeQuery(id+"F1.opExtrude","CAP_EDGE",EDGE,{"disambiguationData":[OSD([sQuery(id+"F0.wireOp",EDGE,"E47")])],"isStart":false});
            var Q50;
            Q50=makeQuery(id+"F1.opExtrude","CAP_EDGE",EDGE,{"disambiguationData":[OSD([sQuery(id+"F0.wireOp",EDGE,"E12")])],"isStart":false});
            var Q51;
            {var subQ3=sQuery(id+"F0.wireOp",EDGE,"E86");var subQ4=sQuery(id+"F0.wireOp",EDGE,"E83");var subQ5=sQuery(id+"F0.wireOp",EDGE,"E82");var subQ6=sQuery(id+"F0.wireOp",EDGE,"E62.trimOffspring");var subQ7=sQuery(id+"F0.wireOp",EDGE,"E61.trimOffspring");var subQ8=sQuery(id+"F0.wireOp",EDGE,"E60.trimOffspring");var subQ9=sQuery(id+"F0.wireOp",EDGE,"E59.trimOffspring");Q51=makeQuery(id+"F3.boolean.opBoolean","SPLIT",EDGE,{"disambiguationData":[TD([makeQuery(id+"F3.opExtrude","SWEPT_FACE",FACE,{"disambiguationData":[OSD([sQuery(id+"F2.wireOp",EDGE,"E100")])]})])],"derivedFrom":makeQuery(id+"F1.opExtrude","CAP_EDGE",EDGE,{"disambiguationData":[OSD([subQ9,subQ8,subQ7,subQ6,subQ5,subQ4,subQ3])],"isStart":false})});}
            chamfer(context, id + "F6", {"entities" : qUnion([Q0, Q1, Q2, Q3, Q4, Q5, Q6, Q7, Q8, Q9, Q10, Q11, Q12, Q13, Q14, Q15, Q16, Q17, Q18, Q19, Q20, Q21, Q22, Q23, Q24, Q25, Q26, Q27, Q28, Q29, Q30, Q31, Q32, Q33, Q34, Q35, Q36, Q37, Q38, Q39, Q40, Q41, Q42, Q43, Q44, Q45, Q46, Q47, Q48, Q49, Q50, Q51]), "width" : 0.64 * mm, "tangentPropagation" : true});
        }
        {
            var Q0;
            Q0=makeQuery(id+"F3.boolean.opBoolean","COPY",FACE,{"derivedFrom":makeQuery(id+"F3.opExtrude","CAP_FACE",FACE,{"disambiguationData":[OSD([sQuery(id+"F2.wireOp",EDGE,"E104"),sQuery(id+"F2.wireOp",EDGE,"E105"),sQuery(id+"F2.wireOp",EDGE,"E106"),sQuery(id+"F2.wireOp",EDGE,"E107")])],"isStart":false})});
            var sketch = newSketch(context, id + "F7", { "sketchPlane" : qUnion([Q0])});
            skLineSegment(sketch, "E109", {"start": v(-128.48, 6.26) * mm, "end": v(-129.69, 6.26) * mm});
            skLineSegment(sketch, "E110", {"start": v(-129.69, 6.26) * mm, "end": v(-131.92, -0.4) * mm});
            skLineSegment(sketch, "E111", {"start": v(-131.92, -0.4) * mm, "end": v(-130.71, -0.4) * mm});
            skLineSegment(sketch, "E112", {"start": v(-130.71, -0.4) * mm, "end": v(-128.48, 6.26) * mm});
            skSolve(sketch);
        }
        {
            var Q0;
            Q0=qSketchRegion(id+"F7",true);
            extrude(context, id + "F8", {"entities" : qUnion([Q0]), "operationType" : NewBodyOperationType.REMOVE, "endBound" : BoundingType.THROUGH_ALL, "oppositeDirection" : true, "depth" : 25.4 * mm, "offsetDistance" : 25.4 * mm});
        }
    });
